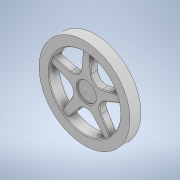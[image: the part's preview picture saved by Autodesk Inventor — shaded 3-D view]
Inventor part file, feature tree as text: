
AUTODESK INVENTOR PART (.ipt)
format: ipt  version: 2022 (Build 260153070, 153G)  size: 412,160 bytes
history: native  units: mm
features: extrude x6, sketch x2, fillet x1
ambient origin geometry x8: Origin, YZ Plane, XZ Plane, XY Plane, X Axis, Y Axis, Z Axis, Center Point
bodies: Solid1 (feature_tree)
feature tree (9):
  extrude  "Extrusion1"  Depth=66.0mm
  sketch  "Sketch2"  dims[d2=8.0mm d3=0.0mm d4=51.8mm d5=13.8mm d6=12.566371mm d7=5.0mm d8=3.5mm d9=5.4mm d10=3.7mm d11=50.0mm d13=360.0deg d15=6.5mm d16=0.0mm d17=8.0mm d18=0.0mm d19=1.25mm d20=0.0mm d21=2.225mm d22=0.0mm d23=0.5mm d27=4.725mm d28=0.0mm]
  extrude  "Extrusion6"  Depth=51.8mm
  extrude  "Extrusion2"  Depth=13.8mm
  extrude  "Extrusion3"  Depth=12.566371mm
  extrude  "Extrusion4"  Depth=5.0mm
  extrude  "Extrusion5"  Depth=3.5mm
  fillet  "Fillet1"  Radius=5.4mm
  sketch  "Sketch1"  dims[d0=51.8mm d1=66.0mm]
